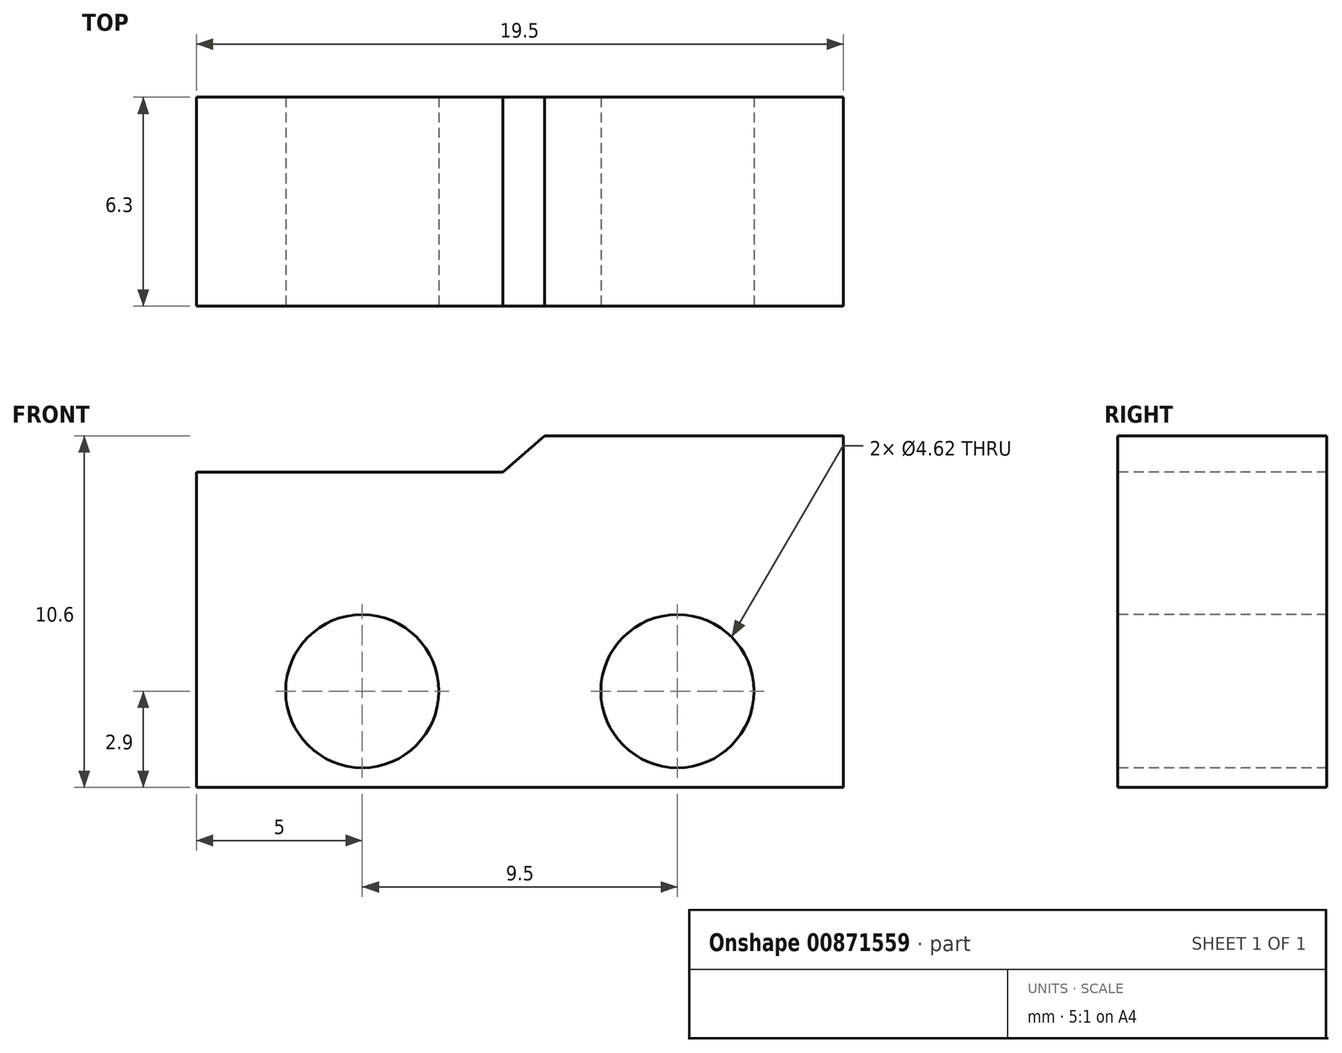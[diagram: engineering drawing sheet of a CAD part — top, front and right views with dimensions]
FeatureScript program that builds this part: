
annotation { "Feature Type Name" : "Feature", "Feature Type Description" : "" }
export const myFeature = defineFeature(function(context is Context, id is Id, definition is map)
    precondition{}
    {
        {
            var Q0;
            Q0=qCreatedBy(makeId("Front.planeOp"),FACE);
            var sketch = newSketch(context, id + "F0", { "sketchPlane" : qUnion([Q0])});
            skLineSegment(sketch, "E0.bottom", {"start": v(0, 0) * mm, "end": v(19.5, 0) * mm});
            skLineSegment(sketch, "E0.top", {"start": v(0, 10.6) * mm, "end": v(19.5, 10.6) * mm});
            skLineSegment(sketch, "E0.left", {"start": v(0, 0) * mm, "end": v(0, 10.6) * mm});
            skLineSegment(sketch, "E0.right", {"start": v(19.5, 0) * mm, "end": v(19.5, 10.6) * mm});
            skSolve(sketch);
        }
        {
            var Q0;
            Q0 = qSketchRegion(id + "F0", true);
            extrude(context, id + "F1", {"entities" : qUnion([Q0]), "depth" : 6.3 * mm, "offsetDistance" : 25 * mm});
        }
        {
            var Q0;
            Q0=makeQuery(id+"F1.opExtrude","CAP_FACE",FACE,{"disambiguationData":[OSD([sQuery(id+"F0.wireOp",EDGE,"E0.bottom"),sQuery(id+"F0.wireOp",EDGE,"E0.top"),sQuery(id+"F0.wireOp",EDGE,"E0.left"),sQuery(id+"F0.wireOp",EDGE,"E0.right")])],"isStart":false});
            var sketch = newSketch(context, id + "F2", { "sketchPlane" : qUnion([Q0])});
            skCircle(sketch, "E1", {"center": v(5, 2.9) * mm, "radius": 2.3 * mm});
            skCircle(sketch, "E2", {"center": v(14.5, 2.9) * mm, "radius": 2.3 * mm});
            skSolve(sketch);
        }
        {
            var Q0;
            Q0 = qSketchRegion(id + "F2", true);
            extrude(context, id + "F3", {"entities" : qUnion([Q0]), "operationType" : NewBodyOperationType.REMOVE, "oppositeDirection" : true, "depth" : 25 * mm, "offsetDistance" : 25 * mm});
        }
        {
            var Q0;
            Q0=makeQuery(id+"F1.opExtrude","CAP_FACE",FACE,{"disambiguationData":[OSD([sQuery(id+"F0.wireOp",EDGE,"E0.bottom"),sQuery(id+"F0.wireOp",EDGE,"E0.top"),sQuery(id+"F0.wireOp",EDGE,"E0.left"),sQuery(id+"F0.wireOp",EDGE,"E0.right")])],"isStart":false});
            var sketch = newSketch(context, id + "F4", { "sketchPlane" : qUnion([Q0])});
            skLineSegment(sketch, "E3", {"start": v(0, 10.6) * mm, "end": v(10.5, 10.6) * mm});
            skLineSegment(sketch, "E4", {"start": v(10.5, 10.6) * mm, "end": v(9.23, 9.5) * mm});
            skLineSegment(sketch, "E5", {"start": v(9.23, 9.5) * mm, "end": v(0, 9.5) * mm});
            skLineSegment(sketch, "E6", {"start": v(0, 9.5) * mm, "end": v(0, 10.6) * mm});
            skSolve(sketch);
        }
        {
            var Q0;
            Q0 = qSketchRegion(id + "F4", true);
            extrude(context, id + "F5", {"entities" : qUnion([Q0]), "operationType" : NewBodyOperationType.REMOVE, "oppositeDirection" : true, "depth" : 25 * mm, "offsetDistance" : 25 * mm});
        }
    });
